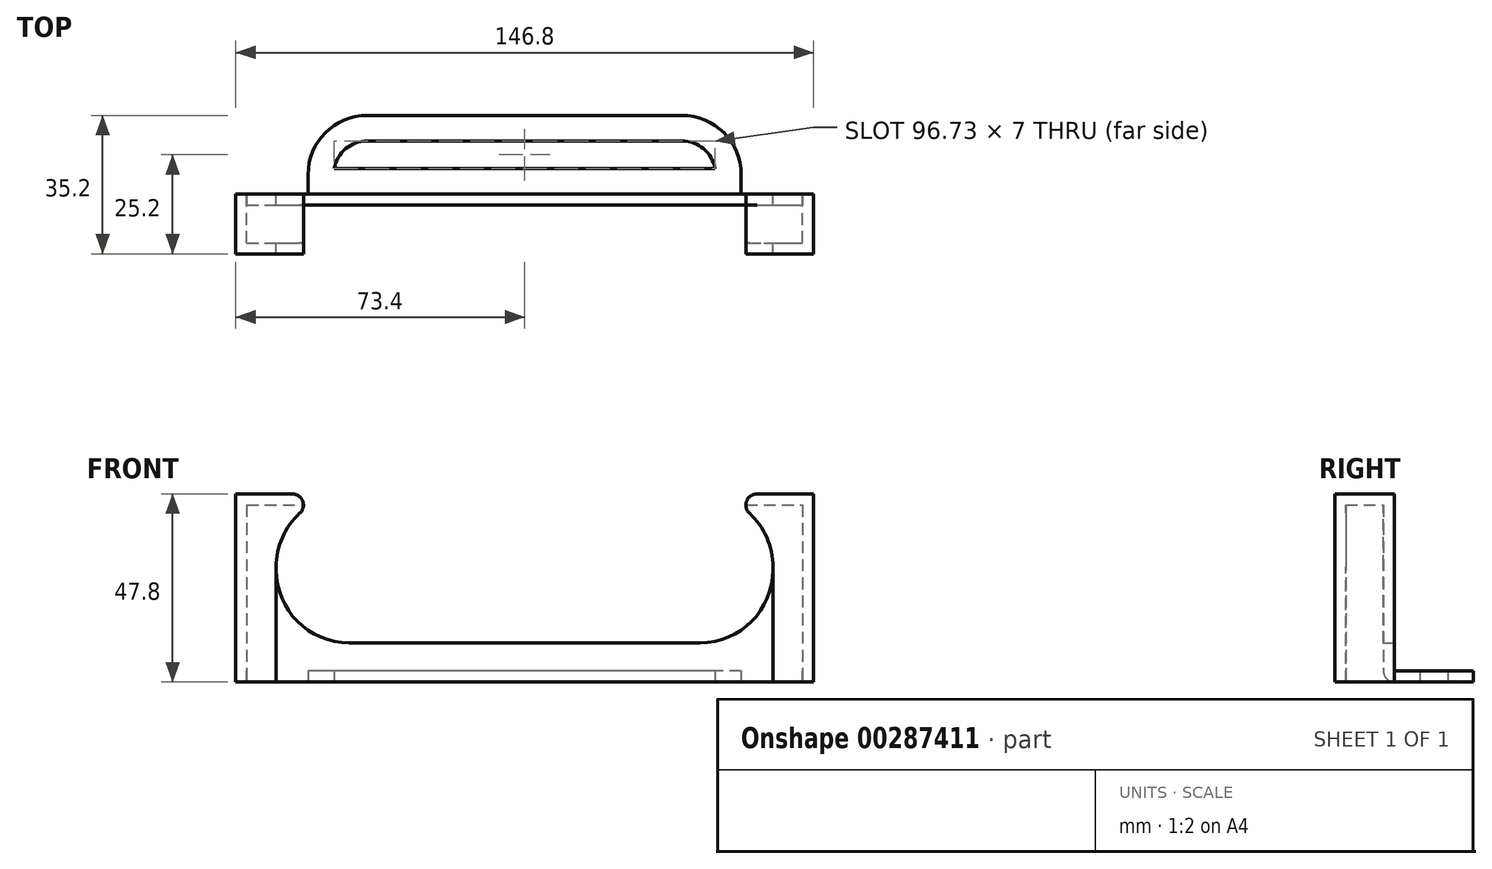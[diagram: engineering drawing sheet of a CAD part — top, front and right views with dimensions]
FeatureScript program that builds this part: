
annotation { "Feature Type Name" : "Feature", "Feature Type Description" : "" }
export const myFeature = defineFeature(function(context is Context, id is Id, definition is map)
    precondition{}
    {
        {
            assignVariable(context, id + "F0", {"name" : "Ancho", "anyValue" : 70});
        }
        {
            assignVariable(context, id + "F1", {"name" : "Grueso", "anyValue" : 9.6});
        }
        {
            assignVariable(context, id + "F2", {"name" : "Pieza", "anyValue" : 2.8});
        }
        {
            var Q0;
            Q0=qCreatedBy(makeId("Top.planeOp"),FACE);
            var sketch = newSketch(context, id + "F3", { "sketchPlane" : qUnion([Q0])});
            skLineSegment(sketch, "E0.top", {"start": v(40, 20) * mm, "end": v(-40, 20) * mm});
            skLineSegment(sketch, "E0.left", {"start": v(55, 0) * mm, "end": v(55, 5) * mm});
            skLineSegment(sketch, "E0.right", {"start": v(-55, 0) * mm, "end": v(-55, 5) * mm});
            skPoint(sketch, "E0.middle", {"position": v(0, 0) * mm});
            skLineSegment(sketch, "E1", {"start": v(55, 0) * mm, "end": v(-55, 0) * mm});
            skPoint(sketch, "E0.bottom.start.orphan", {"position": v(55, -20) * mm});
            skPoint(sketch, "E2.orphan", {"position": v(-55, -20) * mm});
            skPoint(sketch, "E3.visualSharp", {"position": v(55, 20) * mm});
            skArc(sketch, "E3.filletArc", {"start": v(55, 5) * mm, "mid": v(50.6, 15.6) * mm, "end": v(40, 20) * mm});
            skPoint(sketch, "E4.visualSharp", {"position": v(-55, 20) * mm});
            skArc(sketch, "E4.filletArc", {"start": v(-40, 20) * mm, "mid": v(-50.6, 15.6) * mm, "end": v(-55, 5) * mm});
            skArc(sketch, "E5.0", {"start": v(-40, 13.5) * mm, "mid": v(-45.45, 11.52) * mm, "end": v(-48.37, 6.5) * mm});
            skLineSegment(sketch, "E5.1", {"start": v(40, 13.5) * mm, "end": v(-40, 13.5) * mm});
            skArc(sketch, "E5.2", {"start": v(48.37, 6.5) * mm, "mid": v(45.45, 11.52) * mm, "end": v(40, 13.5) * mm});
            skLineSegment(sketch, "E5.3", {"start": v(48.37, 6.5) * mm, "end": v(-48.37, 6.5) * mm});
            skSolve(sketch);
        }
        {
            var Q0;
            Q0=qSketchRegion(id+"F3",true);
            extrude(context, id + "F4", {"entities" : qUnion([Q0]), "depth" : 2.8 * mm});
        }
        {
            var Q0;
            Q0=qCreatedBy(makeId("Top.planeOp"),FACE);
            var sketch = newSketch(context, id + "F5", { "sketchPlane" : qUnion([Q0])});
            skPoint(sketch, "E6.orphan", {"position": v(-70.6, 9.6) * mm});
            skPoint(sketch, "E7.orphan", {"position": v(70.6, 9.6) * mm});
            skLineSegment(sketch, "E8", {"start": v(0, 0) * mm, "end": v(0, -2.8) * mm, "construction": true});
            skLineSegment(sketch, "E9.bottom", {"start": v(-70.6, -12.4) * mm, "end": v(70.6, -12.4) * mm});
            skLineSegment(sketch, "E9.left", {"start": v(-70.6, -12.4) * mm, "end": v(-70.6, -2.8) * mm});
            skLineSegment(sketch, "E9.right", {"start": v(70.6, -12.4) * mm, "end": v(70.6, -2.8) * mm});
            skPoint(sketch, "E9.middle", {"position": v(0, -2.8) * mm});
            skLineSegment(sketch, "E10", {"start": v(-70.6, -2.8) * mm, "end": v(70.6, -2.8) * mm});
            skPoint(sketch, "E9.top.start.orphan", {"position": v(-70.6, 6.8) * mm});
            skPoint(sketch, "E11.orphan", {"position": v(70.6, 6.8) * mm});
            skLineSegment(sketch, "E12.0", {"start": v(-73.4, 0) * mm, "end": v(73.4, 0) * mm});
            skLineSegment(sketch, "E12.1", {"start": v(-73.4, -15.2) * mm, "end": v(-73.4, 0) * mm});
            skLineSegment(sketch, "E12.2", {"start": v(-73.4, -15.2) * mm, "end": v(73.4, -15.2) * mm});
            skLineSegment(sketch, "E12.3", {"start": v(73.4, -15.2) * mm, "end": v(73.4, 0) * mm});
            skSolve(sketch);
        }
        {
            var Q0;
            Q0=qSketchRegion(id+"F5",true);
            extrude(context, id + "F6", {"entities" : qUnion([Q0]), "operationType" : NewBodyOperationType.ADD, "depth" : (getVariable(context, 'Ancho') / 2 + getVariable(context, 'Pieza') + 10) * mm});
        }
        {
            var Q0;
            Q0=qCreatedBy(makeId("Front.planeOp"),FACE);
            var sketch = newSketch(context, id + "F7", { "sketchPlane" : qUnion([Q0])});
            skLineSegment(sketch, "E13", {"start": v(0, 0) * mm, "end": v(0, 10) * mm, "construction": true});
            skLineSegment(sketch, "E14.bottom", {"start": v(-44.6, 47.8) * mm, "end": v(44.6, 47.8) * mm});
            skLineSegment(sketch, "E14.top", {"start": v(-63.1, -27.8) * mm, "end": v(63.1, -27.8) * mm});
            skPoint(sketch, "E14.middle", {"position": v(0, 10) * mm});
            skLineSegment(sketch, "E15", {"start": v(0, 10) * mm, "end": v(0, 14.86) * mm, "construction": true});
            skPoint(sketch, "E16.orphan", {"position": v(-63.1, 10) * mm});
            skPoint(sketch, "E17.orphan", {"position": v(28.3, 5) * mm});
            skPoint(sketch, "E18.end.orphan", {"position": v(-63.1, 21.06) * mm});
            skPoint(sketch, "E19.orphan", {"position": v(-50.13, 10) * mm});
            skPoint(sketch, "E20.MirrorCS.end.orphan", {"position": v(63.1, 21.06) * mm});
            skPoint(sketch, "E21.orphan", {"position": v(50.13, 10) * mm});
            skLineSegment(sketch, "E22.bottom", {"start": v(-73.4, -27.8) * mm, "end": v(73.4, -27.8) * mm});
            skLineSegment(sketch, "E22.left", {"start": v(-73.4, -27.8) * mm, "end": v(-73.4, 47.8) * mm});
            skLineSegment(sketch, "E22.right", {"start": v(73.4, -27.8) * mm, "end": v(73.4, 47.8) * mm});
            skLineSegment(sketch, "E23", {"start": v(-68.45, 47.8) * mm, "end": v(-68.45, 45) * mm, "construction": true});
            skLineSegment(sketch, "E24", {"start": v(-73.4, 45) * mm, "end": v(73.4, 45) * mm});
            skLineSegment(sketch, "E25.bottom", {"start": v(-63.1, -10) * mm, "end": v(63.1, -10) * mm});
            skLineSegment(sketch, "E25.left", {"start": v(-63.1, -10) * mm, "end": v(-63.1, 10) * mm});
            skLineSegment(sketch, "E25.right", {"start": v(63.1, -10) * mm, "end": v(63.1, 10) * mm});
            skPoint(sketch, "E25.middle", {"position": v(0, 0) * mm});
            skPoint(sketch, "E26.newPointB", {"position": v(-63.1, -27.8) * mm});
            skPoint(sketch, "E27.newPointA", {"position": v(63.1, 10) * mm});
            skPoint(sketch, "E27.newPointB", {"position": v(28.3, -32.8) * mm});
            skPoint(sketch, "E28.newPointB", {"position": v(73.4, 47.8) * mm});
            skPoint(sketch, "E29.newPointA", {"position": v(-63.1, 47.8) * mm});
            skPoint(sketch, "E29.newPointB", {"position": v(-73.4, 47.8) * mm});
            skLineSegment(sketch, "E30", {"start": v(63.1, 47.8) * mm, "end": v(73.4, 47.8) * mm});
            skLineSegment(sketch, "E31", {"start": v(-63.1, 47.8) * mm, "end": v(-73.4, 47.8) * mm});
            skLineSegment(sketch, "E32", {"start": v(44.6, 10) * mm, "end": v(-44.6, 10) * mm});
            skLineSegment(sketch, "E33.bottom", {"start": v(63.1, -27.8) * mm, "end": v(-63.1, -27.8) * mm});
            skLineSegment(sketch, "E33.top", {"start": v(63.1, 47.8) * mm, "end": v(-63.1, 47.8) * mm});
            skLineSegment(sketch, "E33.left", {"start": v(63.1, 28.5) * mm, "end": v(63.1, 29.3) * mm});
            skLineSegment(sketch, "E33.right", {"start": v(-63.1, 28.5) * mm, "end": v(-63.1, 29.3) * mm});
            skArc(sketch, "E34.filletArc", {"start": v(-44.6, 47.8) * mm, "mid": v(-57.68, 42.38) * mm, "end": v(-63.1, 29.3) * mm});
            skPoint(sketch, "E35.visualSharp", {"position": v(63.1, 47.8) * mm});
            skArc(sketch, "E35.filletArc", {"start": v(63.1, 29.3) * mm, "mid": v(57.68, 42.38) * mm, "end": v(44.6, 47.8) * mm});
            skArc(sketch, "E36.filletArc", {"start": v(44.6, 10) * mm, "mid": v(57.68, 15.42) * mm, "end": v(63.1, 28.5) * mm});
            skArc(sketch, "E37.filletArc", {"start": v(-63.1, 28.5) * mm, "mid": v(-57.68, 15.42) * mm, "end": v(-44.6, 10) * mm});
            skLineSegment(sketch, "E38", {"start": v(63.1, 10) * mm, "end": v(63.1, 28.5) * mm});
            skLineSegment(sketch, "E39", {"start": v(-63.1, 10) * mm, "end": v(-63.1, 28.5) * mm});
            skLineSegment(sketch, "E40", {"start": v(63.1, 0) * mm, "end": v(-63.1, 0) * mm});
            skSolve(sketch);
        }
        {
            var Q0;
            {var subQ0=sQuery(id+"F7.wireOp",EDGE,"E34.filletArc");var subQ1=sQuery(id+"F7.wireOp",EDGE,"E24");var subQ2=makeQuery(id+"F7.imprint","INTERSECT",VERTEX,{"derivedFrom":[subQ1,subQ0]});Q0=makeQuery(id+"F7.imprint","IMPRINT",FACE,{"disambiguationData":[TD([[makeQuery(id+"F7.imprint","IMPRINT",EDGE,{"disambiguationData":[TD([[subQ2,-1.0]])],"derivedFrom":subQ1}),1.0]])]});}
            var Q1;
            Q1=makeQuery(id+"F7.imprint","IMPRINT",FACE,{"disambiguationData":[TD([[makeQuery(id+"F7.imprint","IMPRINT",EDGE,{"derivedFrom":sQuery(id+"F7.wireOp",EDGE,"E32")}),1.0]])]});
            var Q2;
            Q2=makeQuery(id+"F7.imprint","IMPRINT",FACE,{"disambiguationData":[TD([[makeQuery(id+"F7.imprint","IMPRINT",EDGE,{"derivedFrom":sQuery(id+"F7.wireOp",EDGE,"E32")}),-1.0]])]});
            extrude(context, id + "F8", {"entities" : qUnion([Q0, Q1, Q2]), "operationType" : NewBodyOperationType.REMOVE, "endBound" : BoundingType.THROUGH_ALL, "depth" : 25 * mm});
        }
        {
            var Q0;
            Q0=makeQuery(id+"F7.imprint","IMPRINT",FACE,{"disambiguationData":[TD([[makeQuery(id+"F7.imprint","IMPRINT",EDGE,{"derivedFrom":sQuery(id+"F7.wireOp",EDGE,"E32")}),1.0]])]});
            extrude(context, id + "F9", {"entities" : qUnion([Q0]), "operationType" : NewBodyOperationType.ADD, "depth" : (getVariable(context, 'Pieza')) * mm});
        }
        {
            var Q0;
            {var subQ7=sQuery(id+"F7.wireOp",EDGE,"E31");Q0=makeQuery(id+"F7.imprint","IMPRINT",FACE,{"disambiguationData":[TD([[makeQuery(id+"F7.imprint","IMPRINT",EDGE,{"derivedFrom":subQ7}),1.0]])]});}
            var Q1;
            {var subQ5=sQuery(id+"F7.wireOp",EDGE,"E30");Q1=makeQuery(id+"F7.imprint","IMPRINT",FACE,{"disambiguationData":[TD([[makeQuery(id+"F7.imprint","IMPRINT",EDGE,{"derivedFrom":subQ5}),-1.0]])]});}
            extrude(context, id + "F10", {"entities" : qUnion([Q0, Q1]), "operationType" : NewBodyOperationType.ADD, "depth" : (getVariable(context, 'Pieza') * 2 + getVariable(context, 'Grueso')) * mm});
        }
        {
            var Q0;
            {var subQ0=sQuery(id+"F7.wireOp",EDGE,"84fa5f57-21c0-44a2-a3bd-ebf6e597b42f0.MirrorCS");var subQ1=sQuery(id+"F5.wireOp",EDGE,"E12.3");var subQ2=sQuery(id+"F5.wireOp",EDGE,"E12.2");Q0=makeQuery(id+"F10.boolean.opBoolean","MERGE",FACE,{"derivedFrom":[makeQuery(id+"F8.boolean.opBoolean","SPLIT",FACE,{"disambiguationData":[TD([makeQuery(id+"F6.opExtrude","SWEPT_FACE",FACE,{"disambiguationData":[OSD([subQ1])]})])],"derivedFrom":makeQuery(id+"F6.opExtrude","SWEPT_FACE",FACE,{"disambiguationData":[OSD([subQ2])]})}),makeQuery(id+"F10.opExtrude","CAP_FACE",FACE,{"disambiguationData":[OSD([subQ0,sQuery(id+"F7.wireOp",EDGE,"E22.top"),sQuery(id+"F7.wireOp",EDGE,"E22.right"),sQuery(id+"F7.wireOp",EDGE,"E24")])],"isStart":false})]});}
            var Q1;
            {var subQ0=sQuery(id+"F7.wireOp",EDGE,"MprOEqSB-y6sx-6PDI-jp3v-53XCFHHbe1Hm");var subQ1=sQuery(id+"F5.wireOp",EDGE,"E12.1");var subQ3=sQuery(id+"F5.wireOp",EDGE,"E12.2");Q1=makeQuery(id+"F10.boolean.opBoolean","MERGE",FACE,{"derivedFrom":[makeQuery(id+"F8.boolean.opBoolean","SPLIT",FACE,{"disambiguationData":[TD([makeQuery(id+"F6.opExtrude","SWEPT_FACE",FACE,{"disambiguationData":[OSD([subQ1])]})])],"derivedFrom":makeQuery(id+"F6.opExtrude","SWEPT_FACE",FACE,{"disambiguationData":[OSD([subQ3])]})}),makeQuery(id+"F10.opExtrude","CAP_FACE",FACE,{"disambiguationData":[OSD([subQ0,sQuery(id+"F7.wireOp",EDGE,"E22.top"),sQuery(id+"F7.wireOp",EDGE,"E22.left"),sQuery(id+"F7.wireOp",EDGE,"E24")])],"isStart":false})]});}
            var Q2;
            {var subQ0=sQuery(id+"F5.wireOp",EDGE,"E10");var subQ2=sQuery(id+"F5.wireOp",EDGE,"E9.right");var subQ3=sQuery(id+"F5.wireOp",EDGE,"E9.left");var subQ6=makeQuery(id+"F6.opExtrude","CAP_EDGE",EDGE,{"disambiguationData":[OSD([subQ0])],"isStart":true});Q2=makeQuery(id+"F9.boolean.opBoolean","MERGE",EDGE,{"derivedFrom":[makeQuery(id+"F8.boolean.opBoolean","SPLIT",EDGE,{"disambiguationData":[TD([makeQuery(id+"F6.opExtrude","SWEPT_FACE",FACE,{"disambiguationData":[OSD([subQ3])]})])],"derivedFrom":subQ6}),makeQuery(id+"F8.boolean.opBoolean","SPLIT",EDGE,{"disambiguationData":[TD([makeQuery(id+"F6.opExtrude","SWEPT_FACE",FACE,{"disambiguationData":[OSD([subQ2])]})])],"derivedFrom":subQ6}),makeQuery(id+"F9.opExtrude","CAP_EDGE",EDGE,{"disambiguationData":[OSD([sQuery(id+"F7.wireOp",EDGE,"SQqUsark-5s4f-Qtzb-WCIM-lyToo0OZBbDV")])],"isStart":false})]});}
            var Q3;
            Q3=makeQuery(id+"F10.opExtrude","SWEPT_EDGE",EDGE,{"disambiguationData":[OSD([sQuery(id+"F7.wireOp",EDGE,"84fa5f57-21c0-44a2-a3bd-ebf6e597b42f0.MirrorCS"),sQuery(id+"F7.wireOp",EDGE,"E22.top")])]});
            var Q4;
            {var subQ0=sQuery(id+"F7.wireOp",EDGE,"84fa5f57-21c0-44a2-a3bd-ebf6e597b42f0.MirrorCS");var subQ1=sQuery(id+"F7.wireOp",EDGE,"83f8e419-48e7-43b1-8f8b-a5dbe3628a650.MirrorCS");var subQ2=sQuery(id+"F7.wireOp",EDGE,"E14.right");Q4=makeQuery(id+"F9.boolean.opBoolean","MERGE",EDGE,{"derivedFrom":[makeQuery(id+"F8.boolean.opBoolean","COPY",EDGE,{"disambiguationData":[TD([makeQuery(id+"F6.opExtrude","SWEPT_FACE",FACE,{"disambiguationData":[OSD([sQuery(id+"F5.wireOp",EDGE,"E10")])]})])],"derivedFrom":makeQuery(id+"F8.opExtrude","SWEPT_EDGE",EDGE,{"disambiguationData":[OSD([subQ2,subQ1,subQ0])]})}),makeQuery(id+"F9.opExtrude","SWEPT_EDGE",EDGE,{"disambiguationData":[OSD([subQ2,subQ1,subQ0])]})]});}
            var Q5;
            Q5=makeQuery(id+"F9.opExtrude","SWEPT_EDGE",EDGE,{"disambiguationData":[OSD([sQuery(id+"F7.wireOp",EDGE,"iI8nw9iE-RQTC-mgEL-6MtT-40mJzBxloIGN"),sQuery(id+"F7.wireOp",EDGE,"83f8e419-48e7-43b1-8f8b-a5dbe3628a650.MirrorCS")])]});
            var Q6;
            Q6=makeQuery(id+"F9.opExtrude","SWEPT_EDGE",EDGE,{"disambiguationData":[OSD([sQuery(id+"F7.wireOp",EDGE,"T1g26kiH-DbwM-Kv8P-dkQ6-yeEiJUL4vrzP"),sQuery(id+"F7.wireOp",EDGE,"6oJBWDt3-SSx8-ECbU-zJEw-ogyGQxZJlkgk")])]});
            var Q7;
            {var subQ0=sQuery(id+"F7.wireOp",EDGE,"MprOEqSB-y6sx-6PDI-jp3v-53XCFHHbe1Hm");var subQ1=sQuery(id+"F7.wireOp",EDGE,"6oJBWDt3-SSx8-ECbU-zJEw-ogyGQxZJlkgk");var subQ2=sQuery(id+"F7.wireOp",EDGE,"E14.left");Q7=makeQuery(id+"F9.boolean.opBoolean","MERGE",EDGE,{"derivedFrom":[makeQuery(id+"F8.boolean.opBoolean","COPY",EDGE,{"disambiguationData":[TD([makeQuery(id+"F6.opExtrude","SWEPT_FACE",FACE,{"disambiguationData":[OSD([sQuery(id+"F5.wireOp",EDGE,"E10")])]})])],"derivedFrom":makeQuery(id+"F8.opExtrude","SWEPT_EDGE",EDGE,{"disambiguationData":[OSD([subQ2,subQ1,subQ0])]})}),makeQuery(id+"F9.opExtrude","SWEPT_EDGE",EDGE,{"disambiguationData":[OSD([subQ2,subQ1,subQ0])]})]});}
            var Q8;
            Q8=makeQuery(id+"F10.opExtrude","SWEPT_EDGE",EDGE,{"disambiguationData":[OSD([sQuery(id+"F7.wireOp",EDGE,"MprOEqSB-y6sx-6PDI-jp3v-53XCFHHbe1Hm"),sQuery(id+"F7.wireOp",EDGE,"E22.top")])]});
            var Q9;
            {var subQ0=sQuery(id+"F7.wireOp",EDGE,"E34.filletArc");var subQ1=sQuery(id+"F7.wireOp",EDGE,"E33.top");var subQ2=sQuery(id+"F5.wireOp",EDGE,"E9.bottom");var subQ6=sQuery(id+"F5.wireOp",EDGE,"E10");var subQ8=makeQuery(id+"F8.opExtrude","SWEPT_EDGE",EDGE,{"disambiguationData":[OSD([subQ1,subQ0])]});Q9=makeQuery(id+"F10.boolean.opBoolean","MERGE",EDGE,{"derivedFrom":[makeQuery(id+"F8.boolean.opBoolean","COPY",EDGE,{"disambiguationData":[TD([makeQuery(id+"F6.opExtrude","SWEPT_FACE",FACE,{"disambiguationData":[OSD([subQ6])]})])],"derivedFrom":subQ8}),makeQuery(id+"F8.boolean.opBoolean","COPY",EDGE,{"disambiguationData":[TD([makeQuery(id+"F6.opExtrude","SWEPT_FACE",FACE,{"disambiguationData":[OSD([subQ2])]})])],"derivedFrom":subQ8}),makeQuery(id+"F10.opExtrude","SWEPT_EDGE",EDGE,{"disambiguationData":[OSD([subQ1,subQ0])]})]});}
            var Q10;
            {var subQ0=sQuery(id+"F7.wireOp",EDGE,"E35.filletArc");var subQ1=sQuery(id+"F7.wireOp",EDGE,"E33.top");var subQ2=sQuery(id+"F5.wireOp",EDGE,"E9.bottom");var subQ5=sQuery(id+"F5.wireOp",EDGE,"E10");var subQ8=makeQuery(id+"F8.opExtrude","SWEPT_EDGE",EDGE,{"disambiguationData":[OSD([subQ1,subQ0])]});Q10=makeQuery(id+"F10.boolean.opBoolean","MERGE",EDGE,{"derivedFrom":[makeQuery(id+"F8.boolean.opBoolean","COPY",EDGE,{"disambiguationData":[TD([makeQuery(id+"F6.opExtrude","SWEPT_FACE",FACE,{"disambiguationData":[OSD([subQ5])]})])],"derivedFrom":subQ8}),makeQuery(id+"F8.boolean.opBoolean","COPY",EDGE,{"disambiguationData":[TD([makeQuery(id+"F6.opExtrude","SWEPT_FACE",FACE,{"disambiguationData":[OSD([subQ2])]})])],"derivedFrom":subQ8}),makeQuery(id+"F10.opExtrude","SWEPT_EDGE",EDGE,{"disambiguationData":[OSD([subQ1,subQ0])]})]});}
            fillet(context, id + "F11", {"entities" : qUnion([Q0, Q1, Q2, Q3, Q4, Q5, Q6, Q7, Q8, Q9, Q10]), "radius" : 2.8 * mm, "tangentPropagation" : true, "allowEdgeOverflow" : false});
        }
    });
